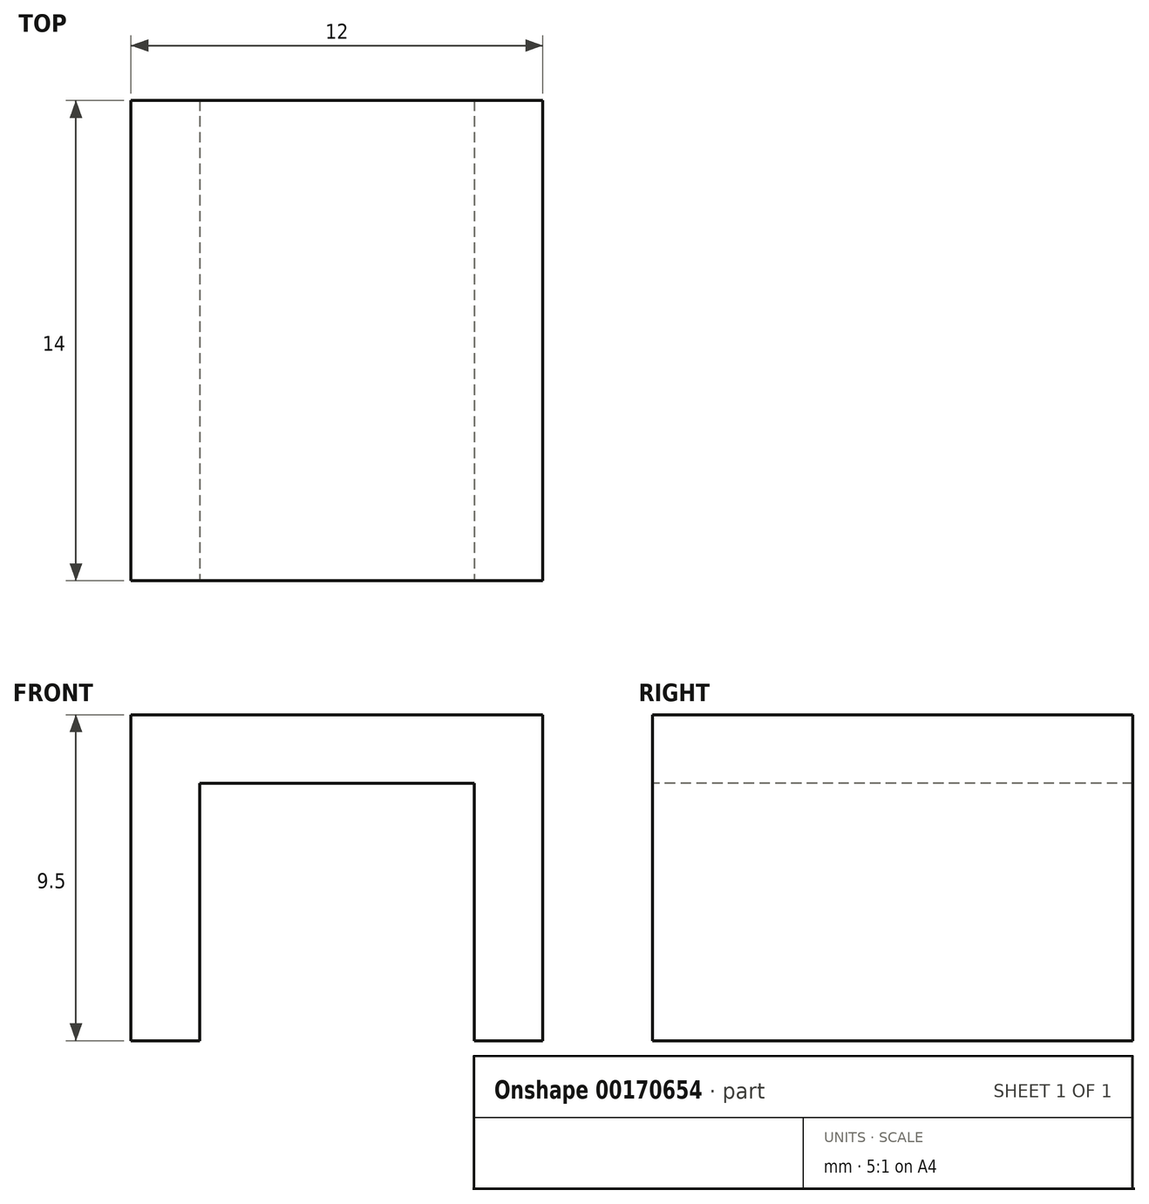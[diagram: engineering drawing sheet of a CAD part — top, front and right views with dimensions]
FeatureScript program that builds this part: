
annotation { "Feature Type Name" : "Feature", "Feature Type Description" : "" }
export const myFeature = defineFeature(function(context is Context, id is Id, definition is map)
    precondition{}
    {
        {
            var Q0;
            Q0=qCreatedBy(makeId("Front.planeOp"),FACE);
            var sketch = newSketch(context, id + "F0", { "sketchPlane" : qUnion([Q0])});
            skLineSegment(sketch, "E0", {"start": v(-4, 0) * mm, "end": v(-6, 0) * mm});
            skLineSegment(sketch, "E1", {"start": v(-4, 0) * mm, "end": v(-4, 7.5) * mm});
            skLineSegment(sketch, "E2", {"start": v(-4, 7.5) * mm, "end": v(0, 7.5) * mm});
            skLineSegment(sketch, "E3", {"start": v(-6, 0) * mm, "end": v(-6, 9.5) * mm});
            skLineSegment(sketch, "E4", {"start": v(-6, 9.5) * mm, "end": v(0, 9.5) * mm});
            skLineSegment(sketch, "E5.MirrorCS", {"start": v(4, 0) * mm, "end": v(6, 0) * mm});
            skLineSegment(sketch, "E6.MirrorCS", {"start": v(4, 7.5) * mm, "end": v(0, 7.5) * mm});
            skLineSegment(sketch, "E7.MirrorCS", {"start": v(6, 9.5) * mm, "end": v(0, 9.5) * mm});
            skLineSegment(sketch, "E8.MirrorCS", {"start": v(4, 0) * mm, "end": v(4, 7.5) * mm});
            skLineSegment(sketch, "E9.MirrorCS", {"start": v(6, 0) * mm, "end": v(6, 9.5) * mm});
            skSolve(sketch);
        }
        {
            var Q0;
            Q0=sQuery(id+"F0.wireOp",EDGE,"E3");
            var Q1;
            Q1=sQuery(id+"F0.wireOp",EDGE,"E4");
            var Q2;
            Q2=sQuery(id+"F0.wireOp",EDGE,"E1");
            var Q3;
            Q3=sQuery(id+"F0.wireOp",EDGE,"E2");
            var Q4;
            Q4=sQuery(id+"F0.wireOp",EDGE,"E6.MirrorCS");
            var Q5;
            Q5=sQuery(id+"F0.wireOp",EDGE,"E7.MirrorCS");
            var Q6;
            Q6=sQuery(id+"F0.wireOp",EDGE,"E8.MirrorCS");
            var Q7;
            Q7=sQuery(id+"F0.wireOp",EDGE,"E9.MirrorCS");
            var Q8;
            Q8=sQuery(id+"F0.wireOp",EDGE,"E0");
            var Q9;
            Q9=sQuery(id+"F0.wireOp",EDGE,"E5.MirrorCS");
            extrude(context, id + "F1", {"bodyType" : ToolBodyType.SURFACE, "surfaceEntities" : qUnion([Q0, Q1, Q2, Q3, Q4, Q5, Q6, Q7, Q8, Q9]), "depth" : 14 * mm});
        }
    });
